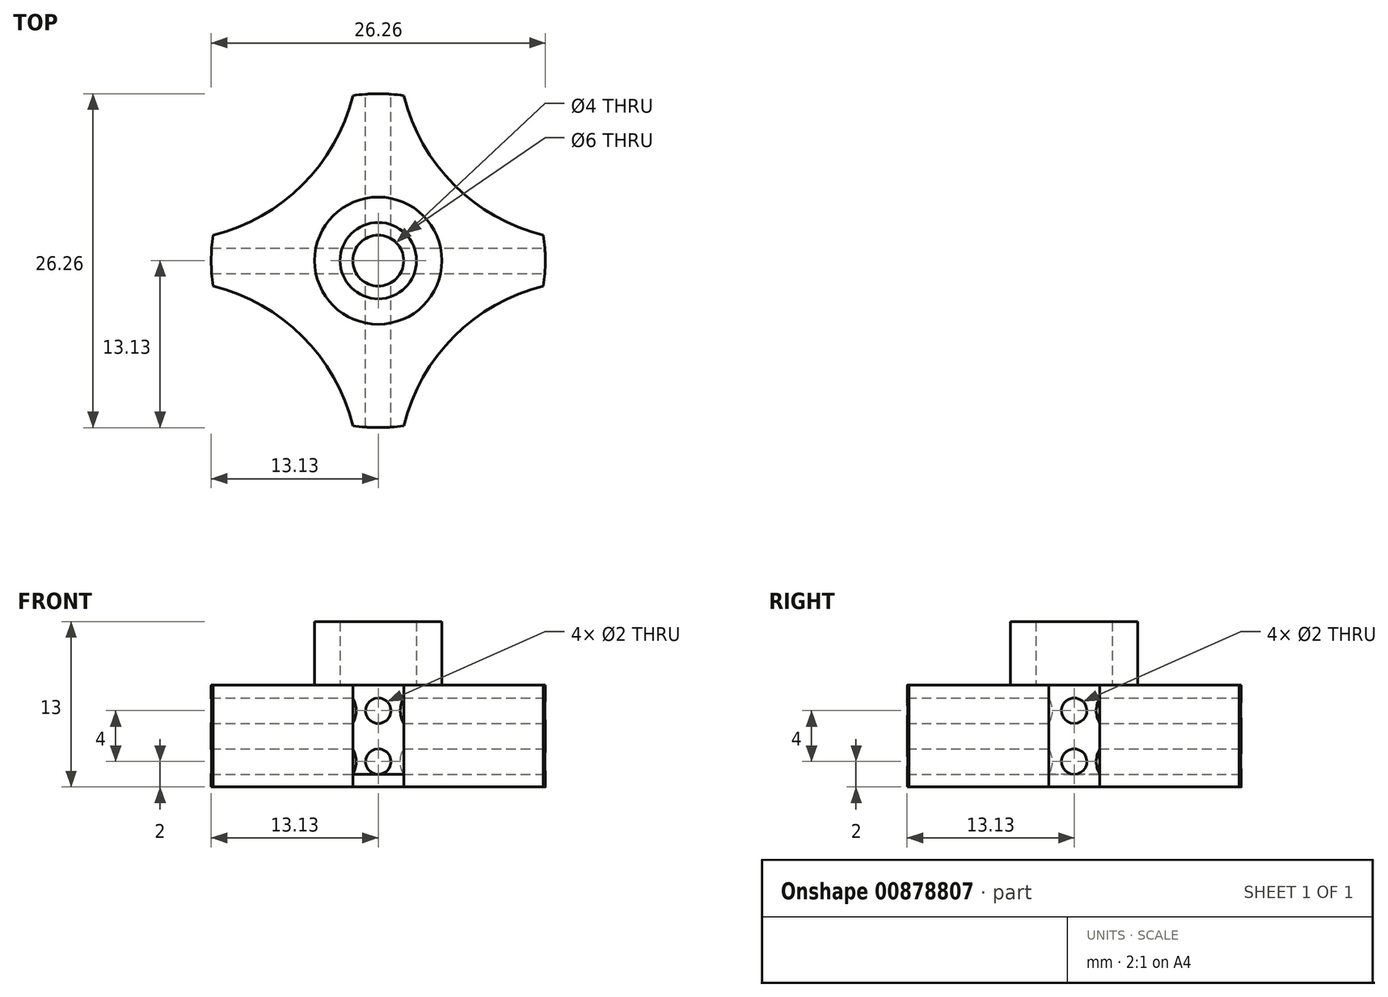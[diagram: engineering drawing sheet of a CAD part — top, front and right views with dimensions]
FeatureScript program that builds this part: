
annotation { "Feature Type Name" : "Feature", "Feature Type Description" : "" }
export const myFeature = defineFeature(function(context is Context, id is Id, definition is map)
    precondition{}
    {
        {
            assignVariable(context, id + "F0", {"name" : "altezza_rialzo", "anyValue" : 5});
        }
        {
            var Q0;
            Q0=qCreatedBy(makeId("Top.planeOp"),FACE);
            var sketch = newSketch(context, id + "F1", { "sketchPlane" : qUnion([Q0])});
            skCircle(sketch, "E0", {"center": v(0, 0) * mm, "radius": 13.12 * mm});
            skCircle(sketch, "E1", {"center": v(0, 0) * mm, "radius": 2 * mm});
            skLineSegment(sketch, "E2", {"start": v(0, 0) * mm, "end": v(2, 0) * mm, "construction": true});
            skLineSegment(sketch, "E3", {"start": v(2, 0) * mm, "end": v(2, -20.96) * mm, "construction": true});
            skLineSegment(sketch, "E4", {"start": v(0, 0) * mm, "end": v(0, -2) * mm, "construction": true});
            skLineSegment(sketch, "E5", {"start": v(0, -2) * mm, "end": v(20.85, -2) * mm, "construction": true});
            skLineSegment(sketch, "E6", {"start": v(0, 0) * mm, "end": v(0, 2) * mm, "construction": true});
            skLineSegment(sketch, "E7", {"start": v(0, 0) * mm, "end": v(-2, 0) * mm, "construction": true});
            skLineSegment(sketch, "E8", {"start": v(-2, 0) * mm, "end": v(-2, -19.76) * mm, "construction": true});
            skLineSegment(sketch, "E9", {"start": v(2, 0) * mm, "end": v(2, 15.42) * mm, "construction": true});
            skLineSegment(sketch, "E10", {"start": v(-2, 0) * mm, "end": v(-2, 13.17) * mm, "construction": true});
            skLineSegment(sketch, "E11", {"start": v(0, -2) * mm, "end": v(-21.6, -2) * mm, "construction": true});
            skLineSegment(sketch, "E12", {"start": v(0, 2) * mm, "end": v(-23.37, 2) * mm, "construction": true});
            skLineSegment(sketch, "E13", {"start": v(0, 2) * mm, "end": v(21.03, 2) * mm, "construction": true});
            skArc(sketch, "E14", {"start": v(12.97, -2) * mm, "mid": v(5.96, -5.96) * mm, "end": v(2, -12.97) * mm});
            skArc(sketch, "E15", {"start": v(2, 12.97) * mm, "mid": v(5.96, 5.96) * mm, "end": v(12.97, 2) * mm});
            skArc(sketch, "E16", {"start": v(-12.97, 2) * mm, "mid": v(-5.96, 5.96) * mm, "end": v(-2, 12.97) * mm});
            skArc(sketch, "E17", {"start": v(-2, -12.97) * mm, "mid": v(-5.96, -5.96) * mm, "end": v(-12.97, -2) * mm});
            skSolve(sketch);
        }
        {
            var Q0;
            Q0=makeQuery(id+"F1.imprint","IMPRINT",FACE,{"disambiguationData":[TD([[makeQuery(id+"F1.imprint","IMPRINT",EDGE,{"derivedFrom":sQuery(id+"F1.wireOp",EDGE,"E1")}),-1.0]])]});
            extrude(context, id + "F2", {"entities" : qUnion([Q0]), "depth" : 8 * mm, "offsetDistance" : 25 * mm});
        }
        {
            var Q0;
            Q0=makeQuery(id+"F1.imprint","IMPRINT",FACE,{"disambiguationData":[TD([[makeQuery(id+"F1.imprint","IMPRINT",EDGE,{"derivedFrom":sQuery(id+"F1.wireOp",EDGE,"E1")}),1.0]])]});
            var Q1;
            Q1=sQuery(id+"F1.wireOp",EDGE,"E1");
            var Q2;
            Q2=sQuery(id+"F1.wireOp",EDGE,"E1");
            extrude(context, id + "F3", {"entities" : qUnion([Q0]), "surfaceEntities" : qUnion([Q1, Q2]), "depth" : 1 * mm, "offsetDistance" : 25 * mm});
        }
        {
            var Q0;
            Q0=qCreatedBy(makeId("Right.planeOp"),FACE);
            var sketch = newSketch(context, id + "F4", { "sketchPlane" : qUnion([Q0])});
            skLineSegment(sketch, "E18", {"start": v(0, 0) * mm, "end": v(0, 2) * mm, "construction": true});
            skCircle(sketch, "E19", {"center": v(0, 2) * mm, "radius": 1 * mm});
            skLineSegment(sketch, "E20", {"start": v(0, 3) * mm, "end": v(0, 6) * mm, "construction": true});
            skCircle(sketch, "E21", {"center": v(0, 6) * mm, "radius": 1 * mm});
            skSolve(sketch);
        }
        {
            var Q0;
            Q0 = qSketchRegion(id + "F4", true);
            extrude(context, id + "F5", {"entities" : qUnion([Q0]), "operationType" : NewBodyOperationType.REMOVE, "oppositeDirection" : true, "depth" : 19 * mm, "offsetDistance" : 25 * mm, "hasSecondDirection" : true, "secondDirectionOppositeDirection" : false, "secondDirectionDepth" : 25 * mm});
        }
        {
            var Q0;
            Q0=qCreatedBy(makeId("Front.planeOp"),FACE);
            var sketch = newSketch(context, id + "F6", { "sketchPlane" : qUnion([Q0])});
            skLineSegment(sketch, "E22", {"start": v(0, 0) * mm, "end": v(0, 2) * mm, "construction": true});
            skCircle(sketch, "E23", {"center": v(0, 2) * mm, "radius": 1 * mm});
            skLineSegment(sketch, "E24", {"start": v(0, 2) * mm, "end": v(0, 6) * mm, "construction": true});
            skCircle(sketch, "E25", {"center": v(0, 6) * mm, "radius": 1 * mm});
            skSolve(sketch);
        }
        {
            var Q0;
            Q0 = qSketchRegion(id + "F6", true);
            extrude(context, id + "F7", {"entities" : qUnion([Q0]), "operationType" : NewBodyOperationType.REMOVE, "depth" : 25 * mm, "offsetDistance" : 25 * mm, "hasSecondDirection" : true, "secondDirectionOppositeDirection" : true, "secondDirectionDepth" : 25 * mm});
        }
        {
            var Q0;
            Q0=qCreatedBy(makeId("Top.planeOp"),FACE);
            var sketch = newSketch(context, id + "F8", { "sketchPlane" : qUnion([Q0])});
            skCircle(sketch, "E26", {"center": v(0, 0) * mm, "radius": 5 * mm});
            skCircle(sketch, "E27", {"center": v(0, 0) * mm, "radius": 3 * mm});
            skSolve(sketch);
        }
        {
            var Q0;
            Q0=makeQuery(id+"F8.imprint","IMPRINT",FACE,{"disambiguationData":[TD([[makeQuery(id+"F8.imprint","IMPRINT",EDGE,{"derivedFrom":sQuery(id+"F8.wireOp",EDGE,"E26")}),1.0]])]});
            extrude(context, id + "F9", {"entities" : qUnion([Q0]), "depth" : (getVariable(context, 'altezza_rialzo')) * mm, "offsetDistance" : 25 * mm});
        }
        {
            var Q0;
            Q0=makeQuery(id+"F9.opExtrude","SWEPT_BODY",BODY,{"disambiguationData":[OSD([sQuery(id+"F8.wireOp",EDGE,"E26")])]});
            transform(context, id + "F10", {"entities" : qUnion([Q0]), "transformType" : TransformType.TRANSLATION_3D, "dx" : 0 * mm, "dy" : 0 * mm, "dz" : 8 * mm, "makeCopy" : false});
        }
    });
